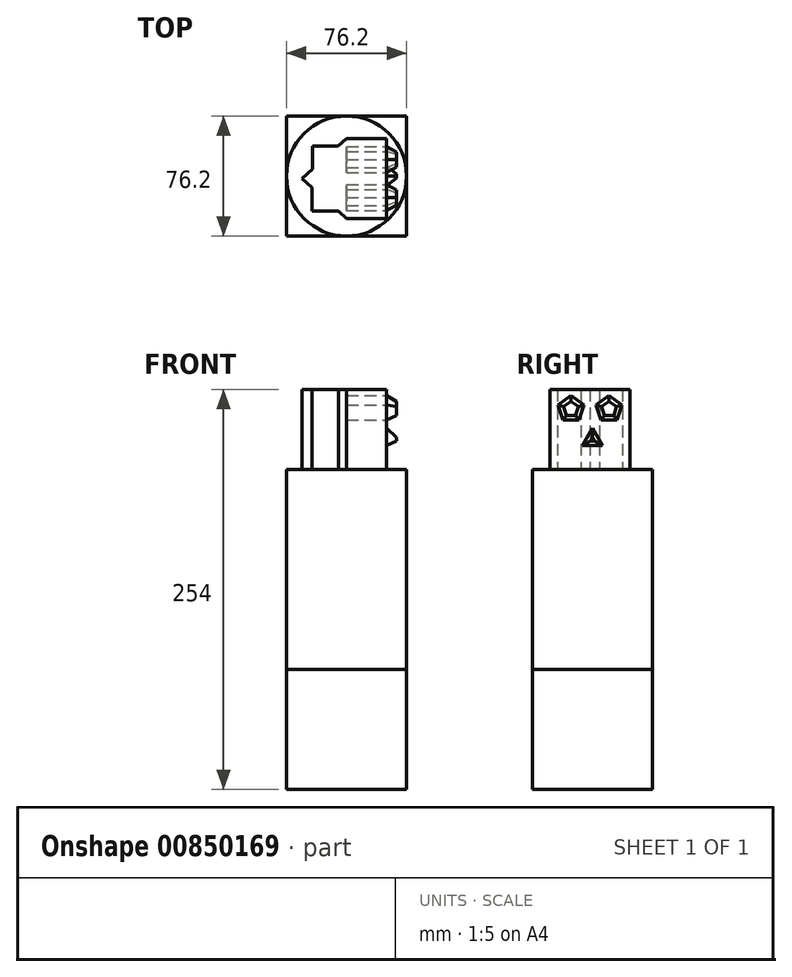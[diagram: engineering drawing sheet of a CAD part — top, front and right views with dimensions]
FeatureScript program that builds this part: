
annotation { "Feature Type Name" : "Feature", "Feature Type Description" : "" }
export const myFeature = defineFeature(function(context is Context, id is Id, definition is map)
    precondition{}
    {
        {
            var Q0;
            Q0=qCreatedBy(makeId("Top.planeOp"),FACE);
            var sketch = newSketch(context, id + "F0", { "sketchPlane" : qUnion([Q0])});
            skLineSegment(sketch, "E0.bottom", {"start": v(38.1, -38.1) * mm, "end": v(-38.1, -38.1) * mm});
            skLineSegment(sketch, "E0.top", {"start": v(38.1, 38.1) * mm, "end": v(-38.1, 38.1) * mm});
            skLineSegment(sketch, "E0.left", {"start": v(38.1, -38.1) * mm, "end": v(38.1, 38.1) * mm});
            skLineSegment(sketch, "E0.right", {"start": v(-38.1, -38.1) * mm, "end": v(-38.1, 38.1) * mm});
            skPoint(sketch, "E0.middle", {"position": v(0, 0) * mm});
            skSolve(sketch);
        }
        {
            var Q0;
            Q0=makeQuery(id+"F0.imprint","IMPRINT",FACE,{"disambiguationData":[TD([[makeQuery(id+"F0.imprint","IMPRINT",EDGE,{"derivedFrom":sQuery(id+"F0.wireOp",EDGE,"E0.bottom")}),-1.0]])]});
            extrude(context, id + "F1", {"entities" : qUnion([Q0]), "depth" : 76.2 * mm, "offsetDistance" : 25.4 * mm});
        }
        {
            var Q0;
            Q0=makeQuery(id+"F1.opExtrude","CAP_FACE",FACE,{"disambiguationData":[OSD([sQuery(id+"F0.wireOp",EDGE,"E0.bottom"),sQuery(id+"F0.wireOp",EDGE,"E0.top"),sQuery(id+"F0.wireOp",EDGE,"E0.left"),sQuery(id+"F0.wireOp",EDGE,"E0.right")])],"isStart":false});
            var sketch = newSketch(context, id + "F2", { "sketchPlane" : qUnion([Q0])});
            skCircle(sketch, "E1", {"center": v(0, 0) * mm, "radius": 38.1 * mm});
            skSolve(sketch);
        }
        {
            var Q0;
            Q0=qSketchRegion(id+"F2",true);
            extrude(context, id + "F3", {"entities" : qUnion([Q0]), "operationType" : NewBodyOperationType.ADD, "depth" : 127 * mm, "offsetDistance" : 25.4 * mm});
        }
        {
            var Q0;
            Q0=makeQuery(id+"F3.opExtrude","CAP_FACE",FACE,{"disambiguationData":[OSD([sQuery(id+"F2.wireOp",EDGE,"E1")])],"isStart":false});
            var sketch = newSketch(context, id + "F4", { "sketchPlane" : qUnion([Q0])});
            skLineSegment(sketch, "E2", {"start": v(0, 23.89) * mm, "end": v(25.4, 23.89) * mm});
            skLineSegment(sketch, "E3", {"start": v(25.4, 23.89) * mm, "end": v(25.4, -26.91) * mm});
            skLineSegment(sketch, "E4", {"start": v(25.4, -26.91) * mm, "end": v(0, -26.91) * mm});
            skLineSegment(sketch, "E5", {"start": v(0, -26.91) * mm, "end": v(-28.4, -1.51) * mm});
            skLineSegment(sketch, "E6", {"start": v(-28.4, -1.51) * mm, "end": v(0, 23.89) * mm});
            skLineSegment(sketch, "E7", {"start": v(-5.56, 18.91) * mm, "end": v(-21.65, 18.91) * mm});
            skLineSegment(sketch, "E8", {"start": v(-21.65, 18.91) * mm, "end": v(-21.65, 4.52) * mm});
            skLineSegment(sketch, "E9", {"start": v(-21.84, -7.38) * mm, "end": v(-21.84, -22.38) * mm});
            skLineSegment(sketch, "E10", {"start": v(-21.84, -22.38) * mm, "end": v(-5.07, -22.38) * mm});
            skSolve(sketch);
        }
        {
            var Q0;
            Q0=makeQuery(id+"F4.imprint","IMPRINT",FACE,{"disambiguationData":[TD([[makeQuery(id+"F4.imprint","IMPRINT",EDGE,{"derivedFrom":sQuery(id+"F4.wireOp",EDGE,"E2")}),-1.0]])]});
            var Q1;
            {var subQ0=sQuery(id+"F4.wireOp",EDGE,"E7");Q1=makeQuery(id+"F4.imprint","IMPRINT",FACE,{"disambiguationData":[TD([[makeQuery(id+"F4.imprint","IMPRINT",EDGE,{"derivedFrom":subQ0}),1.0]])]});}
            var Q2;
            {var subQ0=sQuery(id+"F4.wireOp",EDGE,"E9");Q2=makeQuery(id+"F4.imprint","IMPRINT",FACE,{"disambiguationData":[TD([[makeQuery(id+"F4.imprint","IMPRINT",EDGE,{"derivedFrom":subQ0}),1.0]])]});}
            extrude(context, id + "F5", {"entities" : qUnion([Q0, Q1, Q2]), "depth" : 50.8 * mm, "offsetDistance" : 25.4 * mm});
        }
        {
            var Q0;
            Q0=makeQuery(id+"F5.opExtrude","SWEPT_FACE",FACE,{"disambiguationData":[OSD([sQuery(id+"F4.wireOp",EDGE,"E3")])]});
            var sketch = newSketch(context, id + "F6", { "sketchPlane" : qUnion([Q0])});
            skCircle(sketch, "E11.cCircle", {"center": v(-13.61, 241.55) * mm, "radius": 7 * mm, "construction": true});
            skLineSegment(sketch, "E11.0", {"start": v(-8.53, 234.56) * mm, "end": v(-18.7, 234.56) * mm});
            skLineSegment(sketch, "E11.1", {"start": v(-18.7, 234.56) * mm, "end": v(-21.83, 244.22) * mm});
            skLineSegment(sketch, "E11.2", {"start": v(-21.83, 244.22) * mm, "end": v(-13.61, 250.2) * mm});
            skLineSegment(sketch, "E11.3", {"start": v(-13.61, 250.19) * mm, "end": v(-5.4, 244.22) * mm});
            skLineSegment(sketch, "E11.4", {"start": v(-5.4, 244.22) * mm, "end": v(-8.53, 234.56) * mm});
            skPoint(sketch, "E11.0.midPoint", {"position": v(-13.61, 234.56) * mm});
            skCircle(sketch, "E12.cCircle", {"center": v(10.59, 241.55) * mm, "radius": 7 * mm, "construction": true});
            skLineSegment(sketch, "E12.0", {"start": v(15.67, 234.56) * mm, "end": v(5.5, 234.56) * mm});
            skLineSegment(sketch, "E12.1", {"start": v(5.5, 234.56) * mm, "end": v(2.37, 244.22) * mm});
            skLineSegment(sketch, "E12.2", {"start": v(2.37, 244.22) * mm, "end": v(10.59, 250.2) * mm});
            skLineSegment(sketch, "E12.3", {"start": v(10.59, 250.2) * mm, "end": v(18.8, 244.22) * mm});
            skLineSegment(sketch, "E12.4", {"start": v(18.8, 244.22) * mm, "end": v(15.67, 234.56) * mm});
            skPoint(sketch, "E12.0.midPoint", {"position": v(10.59, 234.56) * mm});
            skCircle(sketch, "E13.cCircle", {"center": v(0, 222.1) * mm, "radius": 3.67 * mm, "construction": true});
            skLineSegment(sketch, "E13.0", {"start": v(6.35, 218.44) * mm, "end": v(-6.35, 218.44) * mm});
            skLineSegment(sketch, "E13.1", {"start": v(-6.35, 218.44) * mm, "end": v(0, 229.44) * mm});
            skLineSegment(sketch, "E13.2", {"start": v(0, 229.44) * mm, "end": v(6.35, 218.44) * mm});
            skPoint(sketch, "E13.0.midPoint", {"position": v(0, 218.44) * mm});
            skSolve(sketch);
        }
        {
            var Q0;
            Q0=makeQuery(id+"F6.imprint","IMPRINT",FACE,{"disambiguationData":[TD([[makeQuery(id+"F6.imprint","IMPRINT",EDGE,{"derivedFrom":sQuery(id+"F6.wireOp",EDGE,"E11.0")}),-1.0]])]});
            var Q1;
            Q1=makeQuery(id+"F6.imprint","IMPRINT",FACE,{"disambiguationData":[TD([[makeQuery(id+"F6.imprint","IMPRINT",EDGE,{"derivedFrom":sQuery(id+"F6.wireOp",EDGE,"E12.0")}),-1.0]])]});
            extrude(context, id + "F7", {"entities" : qUnion([Q0, Q1]), "operationType" : NewBodyOperationType.REMOVE, "oppositeDirection" : true, "depth" : 25.4 * mm, "offsetDistance" : 25.4 * mm});
        }
        {
            var Q0;
            Q0=qSketchRegion(id+"F6",true);
            extrude(context, id + "F8", {"entities" : qUnion([Q0]), "operationType" : NewBodyOperationType.ADD, "depth" : 6.35 * mm, "offsetDistance" : 25.4 * mm, "hasDraft" : true, "draftAngle" : 25 * degree, "draftPullDirection" : true});
        }
    });
